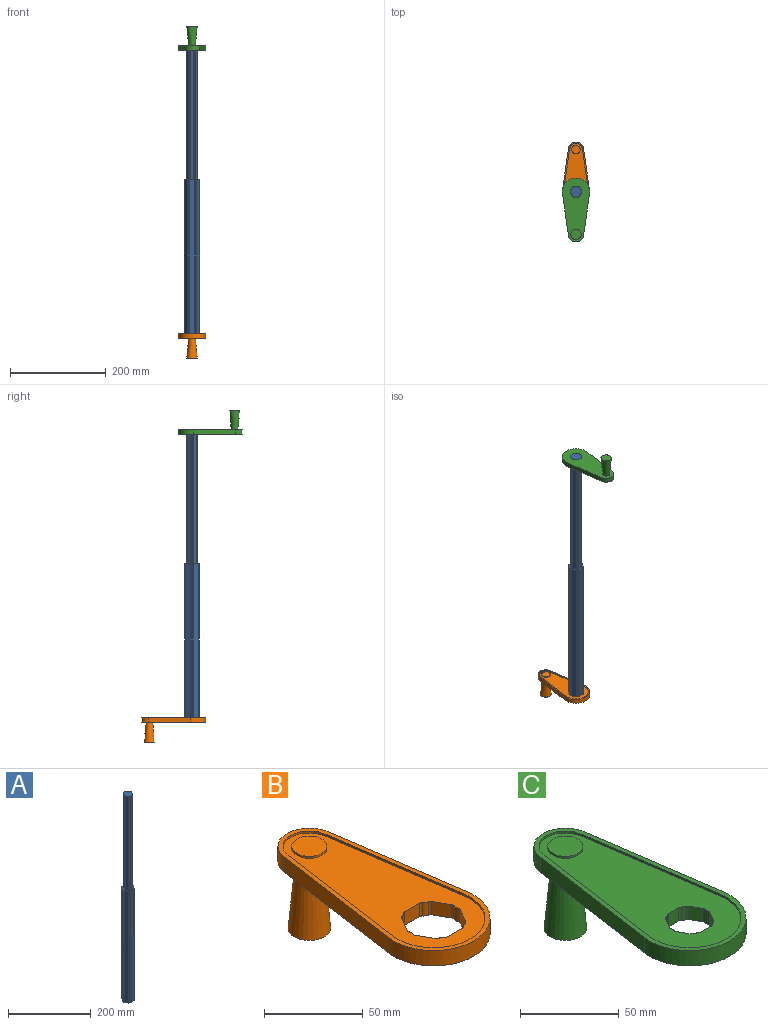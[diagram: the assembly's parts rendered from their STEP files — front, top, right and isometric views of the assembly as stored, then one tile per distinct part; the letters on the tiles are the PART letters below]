
ASSEMBLY  parts=3 mates=2
PART A: 51 faces, bbox 31.5x29.7x609.6 mm
  f0: plane 279.4x6.69mm, normal (-0.87,-0.5,0), area 2157.9mm2, adj f12,f13,f24,f37
  f1: cylinder r=3.17mm len=279.4mm, axis (0,0,-1), area 619.1mm2, adj f12,f13,f14,f37
  f2: plane 279.4x7.72mm, normal (0,-1,0), area 2157.9mm2, adj f12,f14,f15,f37
  f3: cylinder r=3.17mm len=279.4mm, axis (0,0,-1), area 619.1mm2, adj f12,f15,f16,f37
  f4: plane 279.4x6.69mm, normal (0.87,-0.5,0), area 2157.9mm2, adj f12,f16,f17,f37
  f5: cylinder r=3.17mm len=279.4mm, axis (0,0,-1), area 619.1mm2, adj f12,f17,f18,f37
  f6: plane 279.4x6.69mm, normal (0.87,0.5,0), area 2157.9mm2, adj f12,f18,f19,f37
  f7: cylinder r=3.17mm len=279.4mm, axis (0,0,-1), area 619.1mm2, adj f12,f19,f20,f37
  f8: plane 279.4x7.72mm, normal (0,1,0), area 2157.9mm2, adj f12,f20,f21,f37
  f9: cylinder r=3.17mm len=279.4mm, axis (0,0,-1), area 619.1mm2, adj f12,f21,f22,f37
  f10: plane 279.4x6.69mm, normal (-0.87,0.5,0), area 2157.9mm2, adj f12,f22,f23,f37
  f11: cylinder r=3.17mm len=279.4mm, axis (0,0,-1), area 619.1mm2, adj f12,f23,f24,f37
  f12: plane 23.25x22mm, normal (0,0,1), area 404.1mm2, adj f0,f1,f2,f3,f4,f5,f6,f7
  f13: cylinder r=1.27mm len=279.4mm, axis (0,0,-1), area 309.6mm2, adj f0,f1,f12,f37
  f14: cylinder r=1.27mm len=279.4mm, axis (0,0,-1), area 309.6mm2, adj f1,f2,f12,f37
  f15: cylinder r=1.27mm len=279.4mm, axis (0,0,-1), area 309.6mm2, adj f2,f3,f12,f37
  f16: cylinder r=1.27mm len=279.4mm, axis (0,0,-1), area 309.6mm2, adj f3,f4,f12,f37
  f17: cylinder r=1.27mm len=279.4mm, axis (0,0,-1), area 309.6mm2, adj f4,f5,f12,f37
  f18: cylinder r=1.27mm len=279.4mm, axis (0,0,-1), area 309.6mm2, adj f5,f6,f12,f37
  f19: cylinder r=1.27mm len=279.4mm, axis (0,0,-1), area 309.6mm2, adj f6,f7,f12,f37
  f20: cylinder r=1.27mm len=279.4mm, axis (0,0,-1), area 309.6mm2, adj f7,f8,f12,f37
  f21: cylinder r=1.27mm len=279.4mm, axis (0,0,-1), area 309.6mm2, adj f8,f9,f12,f37
  f22: cylinder r=1.27mm len=279.4mm, axis (0,0,-1), area 309.6mm2, adj f9,f10,f12,f37
  f23: cylinder r=1.27mm len=279.4mm, axis (0,0,-1), area 309.6mm2, adj f10,f11,f12,f37
  f24: cylinder r=1.27mm len=279.4mm, axis (0,0,-1), area 309.6mm2, adj f0,f11,f12,f37
  f25: plane 330.2x9.4mm, normal (-0.87,-0.5,0), area 3583mm2, adj f37,f38,f49,f50
  f26: cylinder r=4.29mm len=330.2mm, axis (0,0,-1), area 1091.8mm2, adj f37,f38,f39,f50
  f27: plane 330.2x10.85mm, normal (0,-1,0), area 3583mm2, adj f37,f39,f40,f50
  f28: cylinder r=4.29mm len=330.2mm, axis (0,0,-1), area 1091.8mm2, adj f37,f40,f41,f50
  f29: plane 330.2x9.4mm, normal (0.87,-0.5,0), area 3583mm2, adj f37,f41,f42,f50
  f30: cylinder r=4.29mm len=330.2mm, axis (0,0,-1), area 1091.8mm2, adj f37,f42,f43,f50
  f31: plane 330.2x9.4mm, normal (0.87,0.5,0), area 3583mm2, adj f37,f43,f44,f50
  f32: cylinder r=4.29mm len=330.2mm, axis (0,0,-1), area 1091.8mm2, adj f37,f44,f45,f50
  f33: plane 330.2x10.85mm, normal (0,1,0), area 3583mm2, adj f37,f45,f46,f50
  f34: cylinder r=4.29mm len=330.2mm, axis (0,0,-1), area 1091.8mm2, adj f37,f46,f47,f50
  f35: plane 330.2x9.4mm, normal (-0.87,0.5,0), area 3583mm2, adj f37,f47,f48,f50
  f36: cylinder r=4.29mm len=330.2mm, axis (0,0,-1), area 1091.8mm2, adj f37,f48,f49,f50
  f37: plane 31.48x29.7mm, normal (0,0,1), area 332.9mm2, adj f0,f1,f2,f3,f4,f5,f6,f7
  f38: cylinder r=1.27mm len=330.2mm, axis (0,0,-1), area 381.3mm2, adj f25,f26,f37,f50
  f39: cylinder r=1.27mm len=330.2mm, axis (0,0,-1), area 381.3mm2, adj f26,f27,f37,f50
  f40: cylinder r=1.27mm len=330.2mm, axis (0,0,-1), area 381.3mm2, adj f27,f28,f37,f50
  f41: cylinder r=1.27mm len=330.2mm, axis (0,0,-1), area 381.3mm2, adj f28,f29,f37,f50
  f42: cylinder r=1.27mm len=330.2mm, axis (0,0,-1), area 381.3mm2, adj f29,f30,f37,f50
  f43: cylinder r=1.27mm len=330.2mm, axis (0,0,-1), area 381.3mm2, adj f30,f31,f37,f50
  f44: cylinder r=1.27mm len=330.2mm, axis (0,0,-1), area 381.3mm2, adj f31,f32,f37,f50
  f45: cylinder r=1.27mm len=330.2mm, axis (0,0,-1), area 381.3mm2, adj f32,f33,f37,f50
  f46: cylinder r=1.27mm len=330.2mm, axis (0,0,-1), area 381.3mm2, adj f33,f34,f37,f50
  f47: cylinder r=1.27mm len=330.2mm, axis (0,0,-1), area 381.3mm2, adj f34,f35,f37,f50
  f48: cylinder r=1.27mm len=330.2mm, axis (0,0,-1), area 381.3mm2, adj f35,f36,f37,f50
  f49: cylinder r=1.27mm len=330.2mm, axis (0,0,-1), area 381.3mm2, adj f25,f36,f37,f50
  f50: plane 31.48x29.7mm, normal (0,0,-1), area 737mm2, adj f25,f26,f27,f28,f29,f30,f31,f32
PART B: 39 faces, bbox 57.2x133.4x50.8 mm
  f0: plane 17.78x17.78mm, normal (0,0,1), area 248.3mm2, adj f10
  f1: cylinder r=28.57mm len=57.15mm, axis (0,0,-1), area 933.1mm2, adj f2,f4,f5,f6
  f2: plane 87.09x12.57mm, normal (0.99,0.14,0), area 838.1mm2, adj f1,f3,f5,f6
  f3: cylinder r=15.88mm len=31.42mm, axis (0,0,-1), area 431.7mm2, adj f2,f4,f5,f6
  f4: plane 87.09x12.57mm, normal (-0.99,0.14,0), area 838.1mm2, adj f1,f3,f5,f6
  f5: plane 133.35x57.15mm, normal (0,0,1), area 790.7mm2, adj f1,f2,f3,f4,f7,f8,f9,f11
  f6: plane 133.35x57.15mm, normal (0,0,-1), area 4720.3mm2, adj f1,f2,f3,f4,f14,f15,f16,f17
  f7: plane 87.09x12.57mm, normal (0.99,-0.14,0), area 111.7mm2, adj f5,f8,f11,f12
  f8: cylinder r=26.04mm len=52.07mm, axis (0,0,1), area 113.4mm2, adj f5,f7,f9,f12
  f9: plane 87.09x12.57mm, normal (-0.99,-0.14,0), area 111.7mm2, adj f5,f8,f11,f12
  f10: cylinder r=8.89mm len=17.78mm, axis (0,0,1), area 70.9mm2, adj f0,f12
  f11: cylinder r=13.33mm len=26.4mm, axis (0,0,1), area 48.3mm2, adj f5,f7,f9,f12
  f12: plane 128.27x52.07mm, normal (0,0,1), area 3843.5mm2, adj f7,f8,f9,f10,f11,f15,f16,f17
  f13: plane 21.59x21.59mm, normal (0,0,-1), area 366.1mm2, adj f14
  f14: cone r=6.35mm half-angle=5deg, axis (0,0,-1), area 2340.1mm2, adj f6,f13
  f15: plane 9.4x8.26mm, normal (0.87,0.5,0), area 89.6mm2, adj f6,f12,f27,f38
  f16: cylinder r=3.78mm len=8.26mm, axis (0,0,-1), area 24.1mm2, adj f6,f12,f27,f28
  f17: plane 10.85x8.26mm, normal (0,1,0), area 89.6mm2, adj f6,f12,f28,f29
  f18: cylinder r=3.78mm len=8.26mm, axis (0,0,-1), area 24.1mm2, adj f6,f12,f29,f30
  f19: plane 9.4x8.26mm, normal (-0.87,0.5,0), area 89.6mm2, adj f6,f12,f30,f31
  f20: cylinder r=3.78mm len=8.26mm, axis (0,0,-1), area 24.1mm2, adj f6,f12,f31,f32
  f21: plane 9.4x8.26mm, normal (-0.87,-0.5,0), area 89.6mm2, adj f6,f12,f32,f33
  f22: cylinder r=3.78mm len=8.26mm, axis (0,0,-1), area 24.1mm2, adj f6,f12,f33,f34
  f23: plane 10.85x8.26mm, normal (0,-1,0), area 89.6mm2, adj f6,f12,f34,f35
  f24: cylinder r=3.78mm len=8.26mm, axis (0,0,-1), area 24.1mm2, adj f6,f12,f35,f36
  f25: plane 9.4x8.26mm, normal (0.87,-0.5,0), area 89.6mm2, adj f6,f12,f36,f37
  f26: cylinder r=3.78mm len=8.26mm, axis (0,0,-1), area 24.1mm2, adj f6,f12,f37,f38
  f27: cylinder r=1.78mm len=8.26mm, axis (0,0,-1), area 13.3mm2, adj f6,f12,f15,f16
  f28: cylinder r=1.78mm len=8.26mm, axis (0,0,-1), area 13.3mm2, adj f6,f12,f16,f17
  f29: cylinder r=1.78mm len=8.26mm, axis (0,0,-1), area 13.3mm2, adj f6,f12,f17,f18
  f30: cylinder r=1.78mm len=8.26mm, axis (0,0,-1), area 13.3mm2, adj f6,f12,f18,f19
  f31: cylinder r=1.78mm len=8.26mm, axis (0,0,-1), area 13.3mm2, adj f6,f12,f19,f20
  f32: cylinder r=1.78mm len=8.26mm, axis (0,0,-1), area 13.3mm2, adj f6,f12,f20,f21
  f33: cylinder r=1.78mm len=8.26mm, axis (0,0,-1), area 13.3mm2, adj f6,f12,f21,f22
  f34: cylinder r=1.78mm len=8.26mm, axis (0,0,-1), area 13.3mm2, adj f6,f12,f22,f23
  f35: cylinder r=1.78mm len=8.26mm, axis (0,0,-1), area 13.3mm2, adj f6,f12,f23,f24
  f36: cylinder r=1.78mm len=8.26mm, axis (0,0,-1), area 13.3mm2, adj f6,f12,f24,f25
  f37: cylinder r=1.78mm len=8.26mm, axis (0,0,-1), area 13.3mm2, adj f6,f12,f25,f26
  f38: cylinder r=1.78mm len=8.26mm, axis (0,0,-1), area 13.3mm2, adj f6,f12,f15,f26
PART C: 39 faces, bbox 57.2x133.4x50.8 mm
  f0: plane 133.35x57.15mm, normal (0,0,-1), area 5066.4mm2, adj f2,f3,f4,f5,f14,f15,f16,f17
  f1: plane 17.78x17.78mm, normal (0,0,1), area 248.3mm2, adj f10
  f2: cylinder r=28.57mm len=57.15mm, axis (0,0,-1), area 933.1mm2, adj f0,f3,f5,f6
  f3: plane 87.09x12.57mm, normal (0.99,0.14,0), area 838.1mm2, adj f0,f2,f4,f6
  f4: cylinder r=15.88mm len=31.42mm, axis (0,0,-1), area 431.7mm2, adj f0,f3,f5,f6
  f5: plane 87.09x12.57mm, normal (-0.99,0.14,0), area 838.1mm2, adj f0,f2,f4,f6
  f6: plane 133.35x57.15mm, normal (0,0,1), area 790.7mm2, adj f2,f3,f4,f5,f7,f8,f9,f11
  f7: plane 87.09x12.57mm, normal (0.99,-0.14,0), area 111.7mm2, adj f6,f8,f11,f12
  f8: cylinder r=26.04mm len=52.07mm, axis (0,0,1), area 113.4mm2, adj f6,f7,f9,f12
  f9: plane 87.09x12.57mm, normal (-0.99,-0.14,0), area 111.7mm2, adj f6,f8,f11,f12
  f10: cylinder r=8.89mm len=17.78mm, axis (0,0,1), area 70.9mm2, adj f1,f12
  f11: cylinder r=13.33mm len=26.4mm, axis (0,0,1), area 48.3mm2, adj f6,f7,f9,f12
  f12: plane 128.27x52.07mm, normal (0,0,1), area 4189.5mm2, adj f7,f8,f9,f10,f11,f15,f16,f17
  f13: plane 21.59x21.59mm, normal (0,0,-1), area 366.1mm2, adj f14
  f14: cone r=6.35mm half-angle=5deg, axis (0,0,-1), area 2340.1mm2, adj f0,f13
  f15: plane 8.26x6.69mm, normal (0.87,0.5,0), area 63.8mm2, adj f0,f12,f27,f38
  f16: cylinder r=2.67mm len=8.26mm, axis (0,0,-1), area 15.4mm2, adj f0,f12,f27,f28
  f17: plane 8.26x7.72mm, normal (0,1,0), area 63.8mm2, adj f0,f12,f28,f29
  f18: cylinder r=2.67mm len=8.26mm, axis (0,0,-1), area 15.4mm2, adj f0,f12,f29,f30
  f19: plane 8.26x6.69mm, normal (-0.87,0.5,0), area 63.8mm2, adj f0,f12,f30,f31
  f20: cylinder r=2.67mm len=8.26mm, axis (0,0,-1), area 15.4mm2, adj f0,f12,f31,f32
  f21: plane 8.26x6.69mm, normal (-0.87,-0.5,0), area 63.8mm2, adj f0,f12,f32,f33
  f22: cylinder r=2.67mm len=8.26mm, axis (0,0,-1), area 15.4mm2, adj f0,f12,f33,f34
  f23: plane 8.26x7.72mm, normal (0,-1,0), area 63.8mm2, adj f0,f12,f34,f35
  f24: cylinder r=2.67mm len=8.26mm, axis (0,0,-1), area 15.4mm2, adj f0,f12,f35,f36
  f25: plane 8.26x6.69mm, normal (0.87,-0.5,0), area 63.8mm2, adj f0,f12,f36,f37
  f26: cylinder r=2.67mm len=8.26mm, axis (0,0,-1), area 15.4mm2, adj f0,f12,f37,f38
  f27: cylinder r=1.78mm len=8.26mm, axis (0,0,-1), area 12.8mm2, adj f0,f12,f15,f16
  f28: cylinder r=1.78mm len=8.26mm, axis (0,0,-1), area 12.8mm2, adj f0,f12,f16,f17
  f29: cylinder r=1.78mm len=8.26mm, axis (0,0,-1), area 12.8mm2, adj f0,f12,f17,f18
  f30: cylinder r=1.78mm len=8.26mm, axis (0,0,-1), area 12.8mm2, adj f0,f12,f18,f19
  f31: cylinder r=1.78mm len=8.26mm, axis (0,0,-1), area 12.8mm2, adj f0,f12,f19,f20
  f32: cylinder r=1.78mm len=8.26mm, axis (0,0,-1), area 12.8mm2, adj f0,f12,f20,f21
  f33: cylinder r=1.78mm len=8.26mm, axis (0,0,-1), area 12.8mm2, adj f0,f12,f21,f22
  f34: cylinder r=1.78mm len=8.26mm, axis (0,0,-1), area 12.8mm2, adj f0,f12,f22,f23
  f35: cylinder r=1.78mm len=8.26mm, axis (0,0,-1), area 12.8mm2, adj f0,f12,f23,f24
  f36: cylinder r=1.78mm len=8.26mm, axis (0,0,-1), area 12.8mm2, adj f0,f12,f24,f25
  f37: cylinder r=1.78mm len=8.26mm, axis (0,0,-1), area 12.8mm2, adj f0,f12,f25,f26
  f38: cylinder r=1.78mm len=8.26mm, axis (0,0,-1), area 12.8mm2, adj f0,f12,f15,f26
PLACE A at identity
PLACE B at identity
PLACE C rot(axis=(1,0,0),180deg) t=(0,0,609.6)mm
MATE fastened C.f2 <-> A.f12  axis (0,0,1) through (0,0,609.6)mm
MATE fastened B.f1 <-> A.f50  axis (0,0,-1) through (0,0,0)mm
